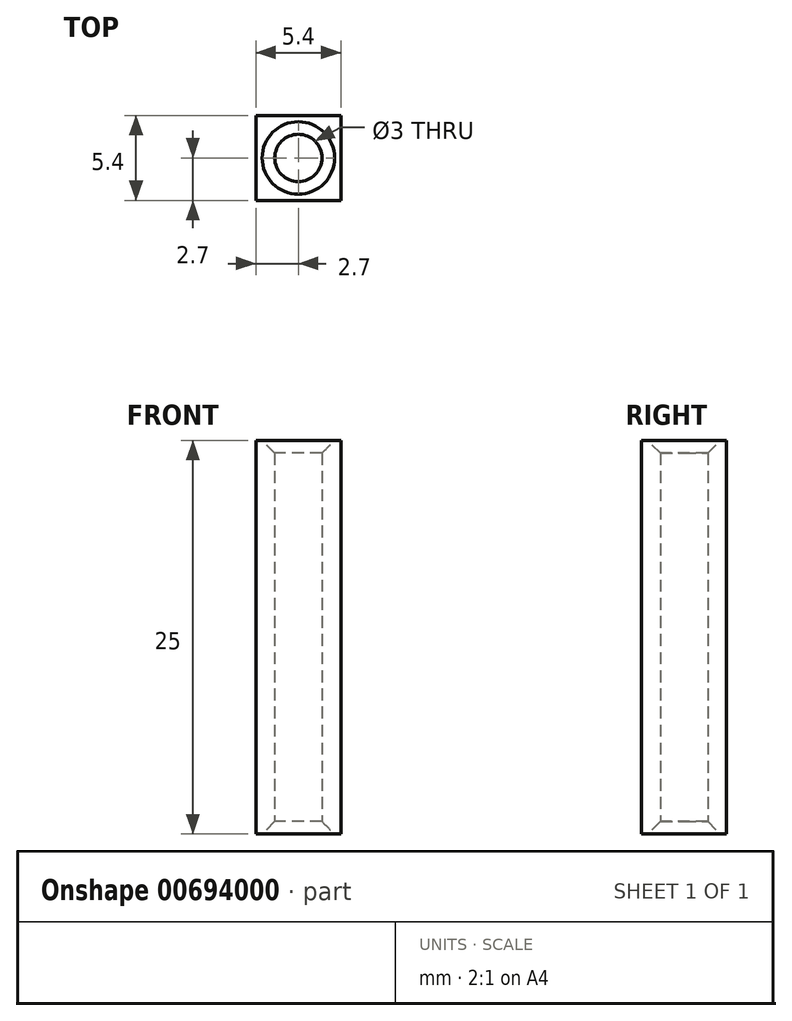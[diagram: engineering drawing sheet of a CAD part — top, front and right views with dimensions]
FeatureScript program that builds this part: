
annotation { "Feature Type Name" : "Feature", "Feature Type Description" : "" }
export const myFeature = defineFeature(function(context is Context, id is Id, definition is map)
    precondition{}
    {
        {
            var Q0;
            Q0=qCreatedBy(makeId("Top.planeOp"),FACE);
            var sketch = newSketch(context, id + "F0", { "sketchPlane" : qUnion([Q0])});
            skCircle(sketch, "E0", {"center": v(0, 0) * mm, "radius": 1.5 * mm});
            skLineSegment(sketch, "E1.bottom", {"start": v(-2.7, 2.7) * mm, "end": v(2.7, 2.7) * mm});
            skLineSegment(sketch, "E1.top", {"start": v(-2.7, -2.7) * mm, "end": v(2.7, -2.7) * mm});
            skLineSegment(sketch, "E1.left", {"start": v(-2.7, 2.7) * mm, "end": v(-2.7, -2.7) * mm});
            skLineSegment(sketch, "E1.right", {"start": v(2.7, 2.7) * mm, "end": v(2.7, -2.7) * mm});
            skSolve(sketch);
        }
        {
            var Q0;
            Q0=makeQuery(id+"F0.imprint","IMPRINT",FACE,{"disambiguationData":[TD([[makeQuery(id+"F0.imprint","IMPRINT",EDGE,{"derivedFrom":sQuery(id+"F0.wireOp",EDGE,"E0")}),-1.0]])]});
            extrude(context, id + "F1", {"entities" : qUnion([Q0]), "depth" : 25 * mm, "offsetDistance" : 25 * mm});
        }
        {
            var Q0;
            Q0=makeQuery(id+"F1.opExtrude","CAP_EDGE",EDGE,{"disambiguationData":[OSD([sQuery(id+"F0.wireOp",EDGE,"E0")])],"isStart":false});
            var Q1;
            Q1=makeQuery(id+"F1.opExtrude","CAP_EDGE",EDGE,{"disambiguationData":[OSD([sQuery(id+"F0.wireOp",EDGE,"E0")])],"isStart":true});
            chamfer(context, id + "F2", {"entities" : qUnion([Q0, Q1]), "width" : 0.8 * mm, "tangentPropagation" : true});
        }
    });
